# Revit family: IEK_БлокГоризонтальный_ОткрытойУстановки_Выключ. двухкл. и роз. одномест. с ЗК 16А IP54_ГЕРМЕС PLUS
name_source: partatom
category: Электрические приборы
units: mm (PartAtom-declared; Revit-internal decimal feet)

## family parameters
Всегда вертикально = Да
На основе рабочей плоскости = Нет
Общий = Нет
При загрузке вырезать с полостями = Нет
Размер круглого соединителя = Использовать диаметр
Сохранять ориентацию аннотаций = Да
Тип детали = Нормальный
Точка расчета площади = Нет

## types (1)
- БГб-22-31-ГПБд
    ADSK_URL страницы изделия = https://www.iek.ru
    ADSK_Версия Revit = 2019
    ADSK_Версия семейства = 1.0
    ADSK_Группирование = III ЭЛЕКТРОУСТАНОВОЧНЫЕ И ЭЛЕКТРОМОНТАЖНЫЕ ИЗДЕЛИЯ
    ADSK_Единица измерения = шт
    ADSK_Завод-изготовитель = IEK
    ADSK_Код изделия = EBGMP20-K03-31-54-EC
    ADSK_Количество фаз = 1
    ADSK_Количество фаз числовое = 1
    ADSK_Марка = ГЕРМЕС PLUS
    ADSK_Масса = 0.22
    ADSK_Материал = Цвет белый
    ADSK_Материал наименование = Пластик
    ADSK_Наименование = Блок горизонтальный для открытой установки БГб-22-31-ГПБд (Выключатель 1-клавишный + розетка 1-местная с заземляющим контактом) IP54 ГЕРМЕС PLUS (белый/дымчатый) IEK
    ADSK_Напряжение = 220 В
    IEK_URL = https://www.iek.ru
    IEK_Описание = Изделия серии "ГЕРМЕС PLUS" используются в помещениях с повышенной влажностью или запыленностью, а также под навесом на открытом воздухе.
    IEK_Цена за единицу = 511.64
    KSI_CMa_Строительные материалы = 01.7.14.03
    KSI_CPr_Строительные изделия = 27.12.31.000.20.2.02.07-1002
    Высота = 72 мм
    Глубина = 52 мм
    Изготовитель = IEK
    Материал крышки = Цвет дымчатый
    Степень защиты = IP54
    Тип монтажа = Поверхность монтажа (открытая установка)
    Ширина = 147 мм
